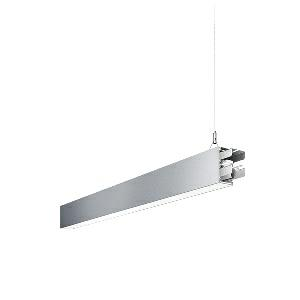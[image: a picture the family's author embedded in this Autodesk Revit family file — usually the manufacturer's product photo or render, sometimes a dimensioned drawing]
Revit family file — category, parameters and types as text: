
# Revit family: idoo_line_-_ilp_3000_840_d_mid_00805692_ec38
name_source: partatom
category: Lighting Fixtures
units: mm (PartAtom-declared; Revit-internal decimal feet)

## family parameters
Cut with Voids When Loaded = No
Host = Face
Light Source = No
Part Type = Normal
Room Calculation Point = No
Round Connector Dimension = Use Diameter
Shared = No

## types (1)
- IDOO.line - ILP 3000/840/D MID (1 x LED, 3150 lm, 4000K)
    Apparent Load = 23 VA
    Approval mark = CE
    CIE Flux Codes = 66 91 98 40 100
    Color Rendering = 80-89
    Color Temperature = 4000K
    Control Gear = Electronic ballast
    Default Elevation = 1800 mm
    Description = ILP 3000/840/D|Suspended luminaire|light source: LED|connected load: 220-240 V, 50/60 Hz|Power consumption: approx. 23 W|standby: approx. 0,20|luminous flux: 3150 lm|luminous efficacy: 136 lm/W|light distribution: Direct/indirect|direct ratio: approx. 40 %|colour temperature: Cold white, ca. 4000 K|color rendering index (CRI): >= 80|chromaticity tolerance:  3 SDCM|System of protection: IP 40|technology: Continuously dimmable|luminaire body|material: Sectional aluminium|colour: Silver|lamp cover: Acrylic (PMMA), Clear|mains lead: 1,0 m With free stranded wires|Fastening: Steel cable 0.3 - 0.7 m|glare control: Prism aperture|luminance(L65): <= 2700 cd/m|unified glare rating(4H 8H): <=  16|special features: DALI Load 1x, TouchDIM - dimming via standard switch, Through-wired, up to 18 m on one mains connection, Flicker-free, Suitable as emergency lighting, Mechanical and electrical connection of the individual modules without tools|
    Frequency = 50 Hz
    Height = 110 mm
    Lamp = 1 x LED
    Lamp Light Flux = 3150 lm
    Lamp count = 1
    Length = 1122 mm
    Luminous efficacy = 137 lm/W
    Manufacturer = Waldmann
    ModVariant = No
    Model = 00805692
    Mounting Place = Ceiling
    Mounting Type = Pendant
    Number of Poles = 1
    OnlyDefault = Yes
    Power Factor = 1
    Product Name = IDOO.line - ILP 3000/840/D MID
    Product group = Suspended luminaire
    ProductGroupID = 9
    Protection Class = Protection class I
    Protection Degree = IP 40
    RLX_Detail_Level = 1
    RLX_Emergency_Light_Flux = 0 lm
    RLX_Emergency_Type = 0
    RLX_Emergency_Type_DB = No
    RlxData = <blob elided: 20913 chars, md5=a3f0eea4>
    Socket = socket
    Standby Power = 0 W
    System Light Flux = 3150 lm
    System Power = 23 W
    Type Comments = Product without accessories
    Type Image = 113305000-00692579.jpg
    URL = http://relux.com
    VarID = ---
    Voltage = 230 V
    Voltage Range = 220-240 V
    Weight = 0.00 kg
    Width = 60 mm  [stored 0.19685 ft]

note: [stored X ft] marks values corroborated as IEEE doubles in the binary element streams (Revit-internal decimal feet)

## geometry (parser evidence)
native form markers: Blend x4, Sweep x13
no freeform markers — native parametric forms only
